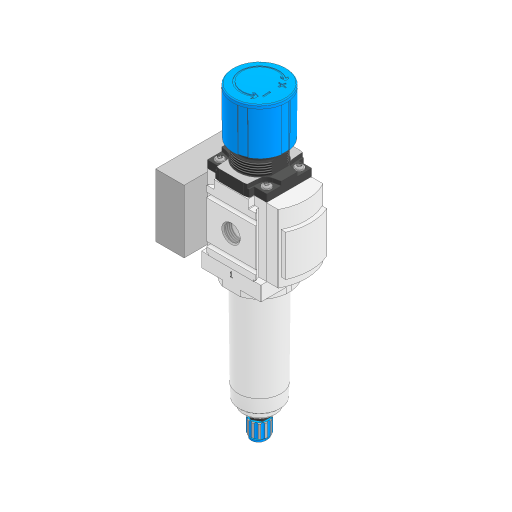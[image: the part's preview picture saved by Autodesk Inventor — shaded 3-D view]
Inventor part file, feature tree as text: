
AUTODESK INVENTOR PART (.ipt)
format: ipt  version: 2024.3 (Build 283343000, 343)  size: 1,356,288 bytes
history: native  units: mm
features: sketch x55, extrude x39, other x14, revolve x12, hole x3, projected_geometry x2, thread x1
ambient origin geometry x8: Origin, YZ Plane, XZ Plane, XY Plane, X Axis, Y Axis, Z Axis, Center Point
bodies: Solid1 (feature_tree)
feature tree (126):
  extrude  "Extrusion1"  Depth=4.5mm TaperAngle=0.0deg
  extrude  "Extrusion2"  Depth=4.5mm TaperAngle=0.0deg
  extrude  "Extrusion3"  Depth=14.2mm TaperAngle=0.0deg
  extrude  "Extrusion4"  Depth=8.2mm TaperAngle=0.0deg
  extrude  "Extrusion5"  Depth=0.4mm TaperAngle=0.0deg
  extrude  "Extrusion6"  Depth=2.75mm TaperAngle=0.0deg
  extrude  "Extrusion7"  TaperAngle=360.0deg  [1 undecoded]
  extrude  "Extrusion8"  TaperAngle=360.0deg  [1 undecoded]
  extrude  "Extrusion9"  Depth=0.92mm TaperAngle=0.0deg
  extrude  "Extrusion10"  Depth=0.92mm TaperAngle=0.0deg
  extrude  "Extrusion11"  TaperAngle=360.0deg  [1 undecoded]
  extrude  "Extrusion12"  Depth=9.13mm TaperAngle=0.0deg
  extrude  "Extrusion13"  Depth=30.5mm TaperAngle=0.0deg
  revolve  "Revolution1"  [1 undecoded]
  revolve  "Revolution2"  [1 undecoded]
  revolve  "Revolution3"  [1 undecoded]
  revolve  "Revolution4"  Angle=360.0deg
  extrude  "Extrusion14"  TaperAngle=360.0deg  [1 undecoded]
  extrude  "Extrusion15"  Depth=10.0mm TaperAngle=0.0deg
  extrude  "Extrusion16"  Depth=48.0mm TaperAngle=0.0deg
  extrude  "Extrusion17"  Depth=1.5mm TaperAngle=0.0deg
  revolve  "Revolution5"  [1 undecoded]
  thread  "Thread1"  [1 undecoded]
  extrude  "Extrusion18"  TaperAngle=360.0deg  [1 undecoded]
  extrude  "Extrusion19"  TaperAngle=360.0deg  [1 undecoded]
  extrude  "Extrusion20"  Depth=1.7mm TaperAngle=0.0deg
  extrude  "Extrusion21"  TaperAngle=0.0deg  [1 undecoded]
  extrude  "Extrusion22"  Depth=64.4mm
  extrude  "Extrusion23"  Depth=52.4mm
  extrude  "Extrusion24"  [1 undecoded]
  extrude  "Extrusion25"  [1 undecoded]
  extrude  "Extrusion26"  [1 undecoded]
  extrude  "Extrusion27"  [1 undecoded]
  revolve  "Revolution6"  [1 undecoded]
  revolve  "Revolution7"  [1 undecoded]
  revolve  "Revolution8"  [1 undecoded]
  revolve  "Revolution9"  [1 undecoded]
  hole  "Hole1"  [1 undecoded]
  hole  "Hole2"  [1 undecoded]
  extrude  "Extrusion28"  [1 undecoded]
  extrude  "Extrusion29"  [1 undecoded]
  extrude  "Extrusion30"  [1 undecoded]
  extrude  "Extrusion31"  [1 undecoded]
  extrude  "Extrusion32"  [1 undecoded]
  extrude  "Extrusion33"  [1 undecoded]
  extrude  "Extrusion34"  [1 undecoded]
  extrude  "Extrusion35"  [1 undecoded]
  revolve  "Revolution10"  [1 undecoded]
  revolve  "Revolution11"  [1 undecoded]
  extrude  "Extrusion36"  [1 undecoded]
  revolve  "Revolution12"  [1 undecoded]
  extrude  "Extrusion37"  [1 undecoded]
  extrude  "Extrusion38"  [1 undecoded]
  other  "IP_LINKS_XY"
  other  "IP_LINKS_YZ"
  other  "IP_LINKS_ZX"
  other  "IP_LINKS_X"
  other  "IP_LINKS_Y"
  other  "IP_LINKS_Z"
  other  "IP_LINKS_Center"
  other  "IP_RECHTS_XY"
  other  "IP_RECHTS_YZ"
  other  "IP_RECHTS_ZX"
  other  "IP_RECHTS_X"
  other  "IP_RECHTS_Y"
  other  "IP_RECHTS_Z"
  other  "IP_RECHTS_Center"
  extrude  "Extrusion39"  [1 undecoded]
  sketch  "Sketch54"
  hole  "Hole3"  [1 undecoded]
  sketch  "Sketch_1"  dims[d0=62.5mm d1=0.0mm d2=4.5mm d3=0.0mm]
  sketch  "Sketch_2"  dims[d4=4.5mm d5=0.0mm d6=4.5mm d7=0.0mm]
  sketch  "Sketch_3"  dims[d8=4.5mm d9=0.0mm d10=14.2mm d11=0.0mm]
  sketch  "Sketch_4"  dims[d12=4.0mm d13=0.0mm d14=8.2mm d15=0.0mm]
  sketch  "Sketch_5"  dims[d16=0.4mm d17=0.0mm d18=2.75mm d19=0.0mm]
  sketch  "Sketch_6"  dims[d20=2.75mm d21=0.0mm d22=2.75mm d23=0.0mm]
  sketch  "Sketch_9"  dims[d24=2.75mm d25=0.0mm d26=360.0deg]
  sketch  "Sketch_10"  dims[d27=360.0deg d28=360.0deg]
  sketch  "Sketch_11"  dims[d29=360.0deg d30=0.92mm d31=0.0mm]
  sketch  "Sketch_12"  dims[d32=0.92mm d33=0.0mm d34=0.92mm d35=0.0mm]
  sketch  "Sketch_13"  dims[d36=0.92mm d37=0.0mm d38=360.0deg]
  sketch  "Sketch_14"  dims[d39=7.71mm d40=0.0mm d41=9.13mm d42=0.0mm]
  sketch  "Sketch_15"  dims[d43=30.5mm d44=0.0mm d45=30.5mm d46=0.0mm]
  sketch  "Sketch_16"  dims[d47=30.5mm d48=0.0mm d49=30.5mm d50=0.0mm]
  sketch  "Sketch_17"  dims[d51=30.5mm d52=0.0mm d53=42.6mm d54=0.0mm]
  sketch  "Sketch_19"  dims[d59=42.6mm d60=0.0mm d61=360.0deg]
  sketch  "Sketch_20"  dims[d62=360.0deg d63=360.0deg]
  sketch  "Sketch_18"  dims[d55=42.6mm d56=0.0mm d57=42.6mm d58=0.0mm]
  sketch  "Sketch_21"  dims[d64=360.0deg]
  sketch  "Sketch_22"  dims[d65=11.445mm d66=6.5mm d67=13.157mm d68=2.0mm d69=90.0deg d70=10.0mm d71=0.0mm]
  sketch  "Sketch_23"  dims[d72=11.445mm d73=6.5mm d74=13.157mm d75=2.0mm d76=90.0deg d77=10.0mm d78=0.0mm d79=0.3mm d80=0.0mm]
  sketch  "Sketch_24"  dims[d81=0.3mm d82=0.0mm d83=48.0mm d84=0.0mm]
  sketch  "Sketch_25"  dims[d85=28.9mm d86=0.0mm d87=1.5mm d88=0.0mm]
  sketch  "Sketch_26"  dims[d89=1.3mm d90=0.0mm d91=1.5mm d92=0.0mm d93=9.0mm d94=0.0mm]
  sketch  "Sketch_27"  dims[d95=17.453293mm d96=360.0deg]
  sketch  "Sketch_28"  dims[d97=8.25mm d98=0.0mm d99=360.0deg]
  sketch  "Sketch_29"  dims[d100=10.1mm d101=0.0mm d102=1.7mm d103=0.0mm]
  sketch  "Sketch_30"  dims[d104=0.0mm d105=0.0mm]
  sketch  "Sketch_32"  dims[d108=20.0mm d109=0.0mm d110=52.4mm]
  sketch  "Sketch_33"  dims[d111=36.4mm]
  sketch  "Sketch_34"  dims[d112=4.8mm d113=6.0mm d114=9.4mm d115=2.0mm d116=90.0deg d117=8.0mm d118=0.0mm]
  sketch  "Sketch_35"
  sketch  "Sketch_36"
  sketch  "Sketch_37"
  sketch  "Sketch_38"
  sketch  "Sketch_39"
  sketch  "Sketch37"
  sketch  "Sketch38"
  sketch  "Sketch_40"
  sketch  "Sketch_41"
  sketch  "Sketch_42"
  sketch  "Sketch_43"
  sketch  "Sketch_46"
  sketch  "Sketch_47"
  sketch  "Sketch_48"
  sketch  "Sketch_49"
  sketch  "Sketch_50"
  sketch  "Sketch_31"  dims[d106=44.4mm d107=64.4mm]
  sketch  "Sketch_53"
  sketch  "Sketch_54"
  sketch  "Sketch_55"
  sketch  "Sketch_56"
  sketch  "Sketch53"
  projected_geometry  "Projected Loop1"
  sketch  "Sketch55"
  projected_geometry  "Projected Loop2"
note: 38 required parameter values undecoded (feature->parameter linkage not recoverable at this tier; creation-order binding heuristic only, values carry confidence <= 0.55)